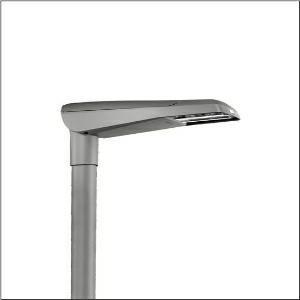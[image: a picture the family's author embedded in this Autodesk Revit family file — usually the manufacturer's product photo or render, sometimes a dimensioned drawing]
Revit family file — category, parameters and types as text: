
# Revit family: streetlight_sl_11_iq_micro___st0_5a_5xc1bc1f08ce_e478
name_source: partatom
category: Lighting Fixtures
units: mm (PartAtom-declared; Revit-internal decimal feet)

## family parameters
Cut with Voids When Loaded = No
Host = Face
Light Source = No
Part Type = Normal
Room Calculation Point = No
Round Connector Dimension = Use Diameter
Shared = No

## types (1)
- --- (1 x LED, 1580 lm, 14 W, 2200K)
    Apparent Load = 14 VA
    CIE Flux Codes = 42 72 97 100 100
    Color Rendering = 70
    Color Temperature = 2200K
    Default Elevation = 1800 mm
    Description = Streetlight SL 11 iQ micro, mast luminaire, primary light control with 3 zone facetted reflector, of plastic, silver coated, highly specular, primary optical cover: cover, of PMMA, transparent, light distribution: ST0.5a, light emission: direct distribution, primary light characteristic: asymmetric, installation type: post-top, side-entry, lamps: LED, High Power LED, rated values: 1.860lm | 13,8W | 134,8lm/W (begin service life); end service life: 1.860lm | 14W; at 50% lumin. flux: 930lm | 7,5W | 124lm/W, colour temperature: 2200/2700/3000/4000K, colour rendering: CRI > 70, light colour: 722/727/730/740, light setting 1 begin service life: 100% | 1.860lm | 13,8W | 134,8lm/W | 3.000K, light setting 1 end service life: 14W, further light settings possible, control: Street-Remote, Auto-Match, Temp-Guard, Lumen-Switch, Night-Set, Smart-Wire, Light-Fading, Desk-Remote (wireless, voltage-free reading and setting of iQ features in the workshop via application-optimized NFC function/RFID function), optimised constant luminous flux control (CLO 2.0), with cable H07RN-F 3x 1.5mm², mains connection: 220..240V, AC, 50/60Hz, connection cable pre-assembled, cable length: 5,5m, luminaire housing, of diecast aluminium, powder-coated, SITECO metallic grey (DB 702S), please order mast flange separately, inclination adjustable without tools: 0°, 5°, 10°, 15° (post-top) | 0°, -5°, -10°, -15° (side-entry), sealing non-destructively replaceable, multi-level sealing system, length: 600mm, width: 174mm, height: 116mm, mast flange for spigot size: 42mm (side-entry): 5XC10008XM4, 60/48mm (side-entry/post-top): 5XC10108XM2, 76/60mm (side-entry/post-top): 5XC10108XM1, equipment: standard, protection rating (complete): IP66, insulation class (complete): insulation class II (safety insulation), certification: CE, ENEC, ENEC+, VDE, impact resistance: IK10, permissible operating ambient temperature for outdoor applications: -25..+50°C, standard-compliant lighting for roads and squares, Environmental Product Declaration (EPD) tested and certified by an independent institute, packaging unit: 1 piece

Light Distribution: ST0.5a
    Height = 116 mm
    Lamp = 1 x LED
    Lamp Light Flux = 1580 lm
    Lamp Power = 14 W
    Lamp count = 1
    Length = 600 mm
    Luminous efficacy = 113 lm/W
    Manufacturer = Siteco
    ModVariant = No
    Model = 5XC1BC1F08CE
    Number of Poles = 1
    OnlyDefault = Yes
    Power Factor = 1
    Product Name = Streetlight SL 11 iQ micro | ST0.5a
    Product group = mast luminaire | pylon top
    ProductGroupID = 6100
    Protection Class = Protection class II
    Protection Degree = IP 66
    RLX_Detail_Level = 1
    RLX_Emergency_Light_Flux = 0 lm
    RLX_Emergency_Type = 0
    RLX_Emergency_Type_DB = No
    RlxData = <blob elided: 58781 chars, md5=47239acc>
    Socket = socket
    Standby Power = 0 W
    System Light Flux = 1580 lm
    System Power = 14 W
    Type Comments = individual setting: luminous flux: 100 % | dim-lin: 254 | 369 mA
    Type Image = l_1006566.jpg
    URL = http://relux.com
    VarID = @adj_042965
    Voltage = 0 V
    Weight = 0.00 kg
    Width = 174 mm

## geometry (parser evidence)
native form markers: Blend x4, Sweep x11
no freeform markers — native parametric forms only
